# Revit family: KM5-Wall Mount
name_source: partatom
category: Lighting Fixtures
revit_build: Autodesk Revit 2013 (Build: 20120221_2030(x64)
units: mm (PartAtom-declared; Revit-internal decimal feet)

## types (1)
- KM51-Wall Mount
    Apparent Load = 50 VA
    Assembly Code = D5020280
    Default Elevation = 48 "
    Description = KM5 brings the performance and features of the full size KicK luminaires into a smaller form factor for architectural pole or building mount applications
    Finish = Hubbell-Titanium
    Glass = Hubbell-Glass
    Lamp = LED
    Load Classification = Lighting
    Manufacturer = Architectural Area Lighting
    Manufacturer Fax = 626-369-2695
    Model = KicK™ Mini Medium-Wall Mount
    Photometrics Web = Web KM5 : KM5-T2-5040
    Power Factor = 1
    Product Documentation Link = http://cdn.aal.net
    Product Page URL = http://www.aal.net
    URL = http://www.aal.net
    Voltage = 120 V
    Watts = 50 W

## geometry (parser evidence)
native form markers: Blend x40, Sweep x4
no freeform markers — native parametric forms only
